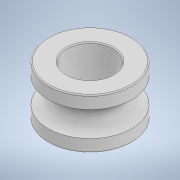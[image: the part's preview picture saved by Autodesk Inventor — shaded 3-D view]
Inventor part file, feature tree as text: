
AUTODESK INVENTOR PART (.ipt)
format: ipt  version: 2021 (Build 250183000, 183)  size: 182,784 bytes
history: native  units: in
note: dims shown in document units (in); Inventor stores cm internally (conversion verified against a paired STEP export)
features: revolve x1, mirror x1, fillet x1, sketch x1
ambient origin geometry x8: Origin, YZ Plane, XZ Plane, XY Plane, X Axis, Y Axis, Z Axis, Center Point
bodies: Solid1 (feature_tree)
feature tree (4):
  revolve  "Revolution1"  [1 undecoded]
  mirror  "Mirror1"
  fillet  "Fillet1"  Radius=0.4331in
  sketch  "Sketch1"  dims[d0=0.7874in d1=0.4724in d2=0.4331in d3=0.0in d4=0.2362in d5=90.0deg d6=0.0197in]
note: 1 required parameter value undecoded (feature->parameter linkage not recoverable at this tier; creation-order binding heuristic only, values carry confidence <= 0.55)
